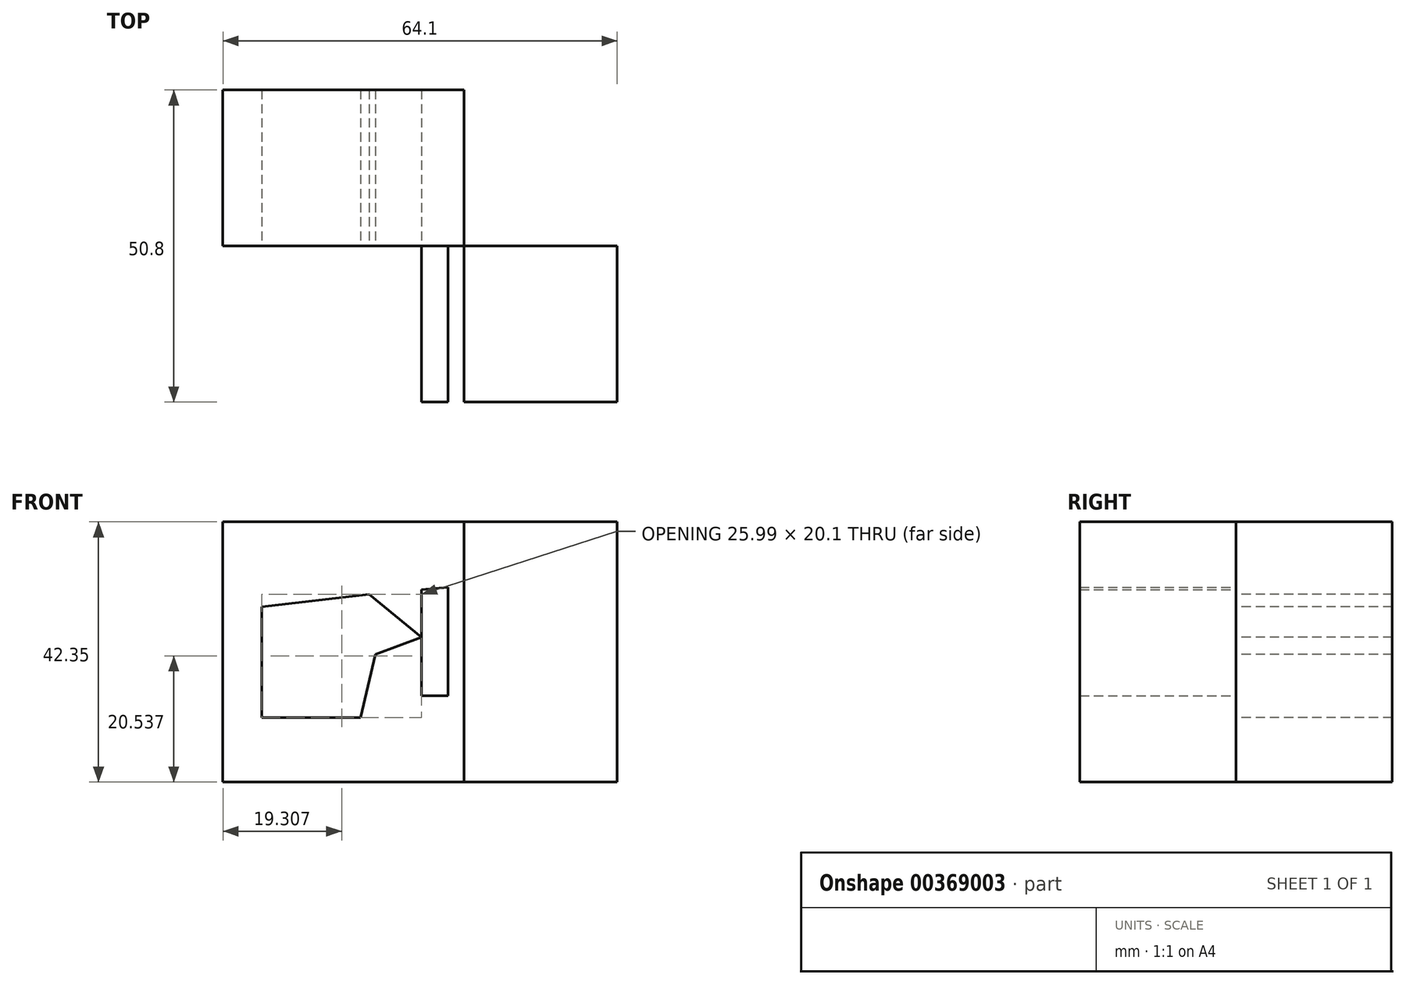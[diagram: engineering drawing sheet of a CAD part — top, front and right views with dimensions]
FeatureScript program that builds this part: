
annotation { "Feature Type Name" : "Feature", "Feature Type Description" : "" }
export const myFeature = defineFeature(function(context is Context, id is Id, definition is map)
    precondition{}
    {
        {
            var Q0;
            Q0=qCreatedBy(makeId("Front.planeOp"),FACE);
            var sketch = newSketch(context, id + "F0", { "sketchPlane" : qUnion([Q0])});
            skLineSegment(sketch, "E0.bottom", {"start": v(0, 0) * mm, "end": v(-39.2, 0) * mm});
            skLineSegment(sketch, "E0.top", {"start": v(0, 42.35) * mm, "end": v(-39.2, 42.35) * mm});
            skLineSegment(sketch, "E0.left", {"start": v(0, 0) * mm, "end": v(0, 42.35) * mm});
            skLineSegment(sketch, "E0.right", {"start": v(-39.2, 0) * mm, "end": v(-39.2, 42.35) * mm});
            skSolve(sketch);
        }
        {
            var Q0;
            Q0 = qSketchRegion(id + "F0", true);
            extrude(context, id + "F1", {"entities" : qUnion([Q0]), "depth" : 25.4 * mm});
        }
        {
            var Q0;
            Q0=makeQuery(id+"F1.opExtrude","CAP_FACE",FACE,{"disambiguationData":[OSD([sQuery(id+"F0.wireOp",EDGE,"E0.bottom"),sQuery(id+"F0.wireOp",EDGE,"E0.top"),sQuery(id+"F0.wireOp",EDGE,"E0.left"),sQuery(id+"F0.wireOp",EDGE,"E0.right")])],"isStart":false});
            var sketch = newSketch(context, id + "F2", { "sketchPlane" : qUnion([Q0])});
            skLineSegment(sketch, "E1", {"start": v(-15.4, 30.59) * mm, "end": v(-32.88, 28.53) * mm});
            skLineSegment(sketch, "E2", {"start": v(-32.88, 28.53) * mm, "end": v(-32.88, 10.49) * mm});
            skLineSegment(sketch, "E3", {"start": v(-32.88, 10.49) * mm, "end": v(-16.78, 10.49) * mm});
            skLineSegment(sketch, "E4", {"start": v(-15.4, 30.59) * mm, "end": v(-6.89, 23.61) * mm});
            skLineSegment(sketch, "E5", {"start": v(-6.89, 23.61) * mm, "end": v(-21.84, 17.92) * mm});
            skLineSegment(sketch, "E6", {"start": v(-16.78, 10.49) * mm, "end": v(-14.36, 20.76) * mm});
            skLineSegment(sketch, "E7", {"start": v(-14.36, 20.76) * mm, "end": v(-20.92, 15.63) * mm});
            skPoint(sketch, "E7.endSnap0", {"position": v(-15.57, 15.63) * mm});
            skLineSegment(sketch, "E8", {"start": v(-21.84, 17.92) * mm, "end": v(-20.92, 15.63) * mm});
            skSolve(sketch);
        }
        {
            var Q0;
            Q0 = qSketchRegion(id + "F2", true);
            extrude(context, id + "F3", {"entities" : qUnion([Q0]), "operationType" : NewBodyOperationType.REMOVE, "oppositeDirection" : true, "depth" : 25.4 * mm});
        }
        {
            var Q0;
            Q0=makeQuery(id+"F1.opExtrude","CAP_FACE",FACE,{"disambiguationData":[OSD([sQuery(id+"F0.wireOp",EDGE,"E0.bottom"),sQuery(id+"F0.wireOp",EDGE,"E0.top"),sQuery(id+"F0.wireOp",EDGE,"E0.left"),sQuery(id+"F0.wireOp",EDGE,"E0.right")])],"isStart":false});
            var sketch = newSketch(context, id + "F4", { "sketchPlane" : qUnion([Q0])});
            skLineSegment(sketch, "E9", {"start": v(-6.89, 23.61) * mm, "end": v(-6.89, 31.3) * mm});
            skLineSegment(sketch, "E10", {"start": v(-6.89, 23.61) * mm, "end": v(-6.89, 14.08) * mm});
            skLineSegment(sketch, "E11", {"start": v(-6.89, 14.08) * mm, "end": v(-2.57, 14.08) * mm});
            skLineSegment(sketch, "E12", {"start": v(-2.57, 14.08) * mm, "end": v(-2.57, 31.74) * mm});
            skLineSegment(sketch, "E13", {"start": v(-2.57, 31.74) * mm, "end": v(-6.89, 31.3) * mm});
            skSolve(sketch);
        }
        {
            var Q0;
            Q0 = qSketchRegion(id + "F4", true);
            extrude(context, id + "F5", {"entities" : qUnion([Q0]), "operationType" : NewBodyOperationType.ADD, "depth" : 25.4 * mm});
        }
        {
            var Q0;
            Q0=makeQuery(id+"F1.opExtrude","CAP_FACE",FACE,{"disambiguationData":[OSD([sQuery(id+"F0.wireOp",EDGE,"E0.bottom"),sQuery(id+"F0.wireOp",EDGE,"E0.top"),sQuery(id+"F0.wireOp",EDGE,"E0.left"),sQuery(id+"F0.wireOp",EDGE,"E0.right")])],"isStart":false});
            var sketch = newSketch(context, id + "F6", { "sketchPlane" : qUnion([Q0])});
            skLineSegment(sketch, "E14.bottom", {"start": v(0, 42.35) * mm, "end": v(24.91, 42.35) * mm});
            skLineSegment(sketch, "E14.top", {"start": v(0, 0) * mm, "end": v(24.91, 0) * mm});
            skLineSegment(sketch, "E14.left", {"start": v(0, 42.35) * mm, "end": v(0, 0) * mm});
            skLineSegment(sketch, "E14.right", {"start": v(24.91, 42.35) * mm, "end": v(24.91, 0) * mm});
            skSolve(sketch);
        }
        {
            var Q0;
            Q0 = qSketchRegion(id + "F6", true);
            extrude(context, id + "F7", {"entities" : qUnion([Q0]), "operationType" : NewBodyOperationType.ADD, "depth" : 25.4 * mm});
        }
    });
